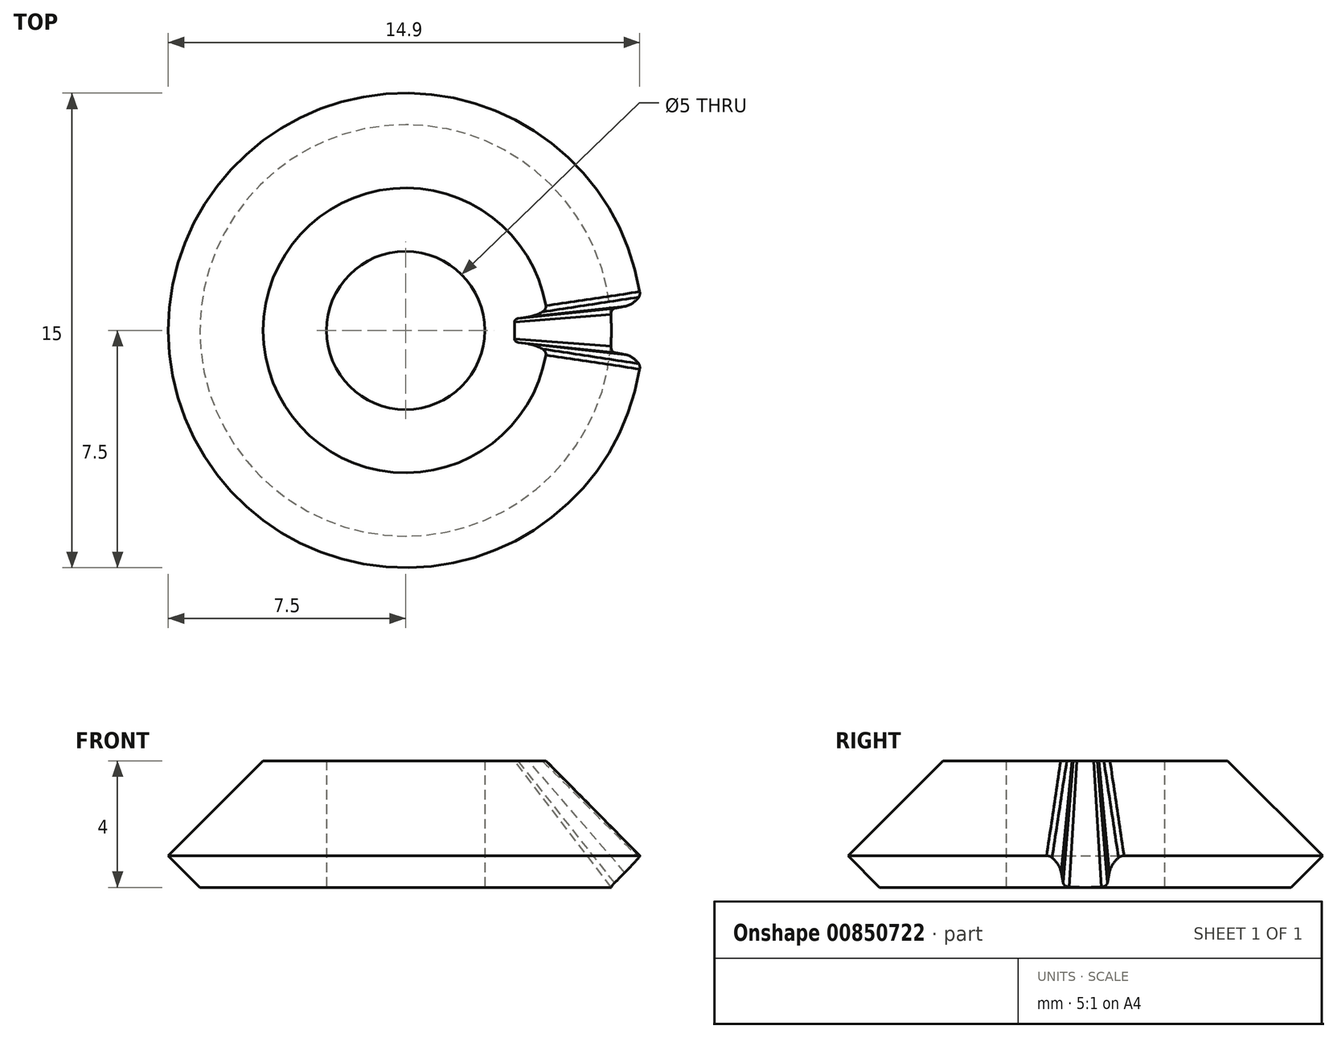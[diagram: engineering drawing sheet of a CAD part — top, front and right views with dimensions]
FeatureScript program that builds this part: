
annotation { "Feature Type Name" : "Feature", "Feature Type Description" : "" }
export const myFeature = defineFeature(function(context is Context, id is Id, definition is map)
    precondition{}
    {
        {
            var Q0;
            Q0=qCreatedBy(makeId("Front.planeOp"),FACE);
            var sketch = newSketch(context, id + "F0", { "sketchPlane" : qUnion([Q0])});
            skLineSegment(sketch, "E0", {"start": v(2.5, 0) * mm, "end": v(6.5, 0) * mm});
            skLineSegment(sketch, "E1", {"start": v(6.5, 0) * mm, "end": v(7.5, 1) * mm});
            skLineSegment(sketch, "E2", {"start": v(7.5, 1) * mm, "end": v(4.5, 4) * mm});
            skLineSegment(sketch, "E3", {"start": v(4.5, 4) * mm, "end": v(2.5, 4) * mm});
            skLineSegment(sketch, "E4", {"start": v(2.5, 4) * mm, "end": v(2.5, 0) * mm});
            skLineSegment(sketch, "E5", {"start": v(8.5, 0) * mm, "end": v(0, 8.5) * mm, "construction": true});
            skLineSegment(sketch, "E6", {"start": v(0, 0) * mm, "end": v(0, 8.5) * mm, "construction": true});
            skLineSegment(sketch, "E7", {"start": v(0, 0) * mm, "end": v(8.5, 0) * mm, "construction": true});
            skSolve(sketch);
        }
        {
            var Q0;
            Q0 = qSketchRegion(id + "F0", true);
            var Q1;
            Q1=sQuery(id+"F0.wireOp",EDGE,"E6");
            revolve(context, id + "F1", {"surfaceOperationType" : NewSurfaceOperationType.NEW, "entities" : qUnion([Q0]), "axis" : qUnion([Q1]), "revolveType" : RevolveType.FULL});
        }
        {
            var Q0;
            Q0=sQuery(id+"F0.wireOp",EDGE,"E5");
            var Q1;
            Q1=sQuery(id+"F0.wireOp",VERTEX,"E1.end");
            cPlane(context, id + "F2", {"entities" : qUnion([Q0, Q1]), "cplaneType" : CPlaneType.LINE_POINT, "offset" : 25 * mm, "width" : 150 * mm, "height" : 150 * mm});
        }
        {
            var Q0;
            Q0=qCreatedBy(id+"F2.planeOp",FACE);
            var sketch = newSketch(context, id + "F3", { "sketchPlane" : qUnion([Q0])});
            skLineSegment(sketch, "E8", {"start": v(0.5, 4.6) * mm, "end": v(-0.5, 4.6) * mm});
            skLineSegment(sketch, "E9", {"start": v(0.7, 4.77) * mm, "end": v(0.76, 5.23) * mm});
            skLineSegment(sketch, "E10", {"start": v(-0.7, 4.77) * mm, "end": v(-0.76, 5.23) * mm});
            skArc(sketch, "E11", {"start": v(1.14, 5.96) * mm, "mid": v(0.89, 5.63) * mm, "end": v(0.76, 5.23) * mm});
            skArc(sketch, "E12", {"start": v(-0.76, 5.23) * mm, "mid": v(-0.89, 5.63) * mm, "end": v(-1.14, 5.96) * mm});
            skArc(sketch, "E13", {"start": v(1.14, 5.96) * mm, "mid": v(0, 6.07) * mm, "end": v(-1.14, 5.96) * mm});
            skPoint(sketch, "E14.visualSharp", {"position": v(0.68, 4.6) * mm});
            skArc(sketch, "E14.filletArc", {"start": v(0.5, 4.6) * mm, "mid": v(0.64, 4.65) * mm, "end": v(0.7, 4.77) * mm});
            skPoint(sketch, "E15.visualSharp", {"position": v(-0.68, 4.6) * mm});
            skArc(sketch, "E15.filletArc", {"start": v(-0.7, 4.77) * mm, "mid": v(-0.64, 4.65) * mm, "end": v(-0.5, 4.6) * mm});
            skSolve(sketch);
        }
        {
            var Q1;
            Q1 = qSketchRegion(id + "F3", true);
            var Q2;
            Q2=sQuery(id+"F0.wireOp",VERTEX,"E5.end");
            loft(context, id + "F4", {"operationType" : NewBodyOperationType.REMOVE, "sheetProfilesArray" : [{ "sheetProfileEntities" : qUnion([Q1]) }, { "sheetProfileEntities" : qUnion([Q2]) }]});
        }
        {
            var Q0;
            Q0=makeQuery(id+"F4.boolean.opBoolean","INTERSECT",EDGE,{"derivedFrom":[makeQuery(id+"F1.opRevolve","SWEPT_FACE",FACE,{"disambiguationData":[OSD([sQuery(id+"F0.wireOp",EDGE,"E2")])]}),makeQuery(id+"F4.opLoft","SWEPT_FACE",FACE,{"disambiguationData":[OSD([sQuery(id+"F3.wireOp",EDGE,"E10"),sQuery(id+"F3.wireOp",EDGE,"E12"),sQuery(id+"F3.wireOp",EDGE,"E13")])]})]});
            var Q1;
            Q1=makeQuery(id+"F4.boolean.opBoolean","INTERSECT",EDGE,{"derivedFrom":[makeQuery(id+"F1.opRevolve","SWEPT_FACE",FACE,{"disambiguationData":[OSD([sQuery(id+"F0.wireOp",EDGE,"E2")])]}),makeQuery(id+"F4.opLoft","SWEPT_FACE",FACE,{"disambiguationData":[OSD([sQuery(id+"F3.wireOp",EDGE,"E9"),sQuery(id+"F3.wireOp",EDGE,"E11"),sQuery(id+"F3.wireOp",EDGE,"E13")])]})]});
            fillet(context, id + "F5", {"entities" : qUnion([Q0, Q1]), "radius" : 0.2 * mm, "tangentPropagation" : true, "allowEdgeOverflow" : false});
        }
    });
